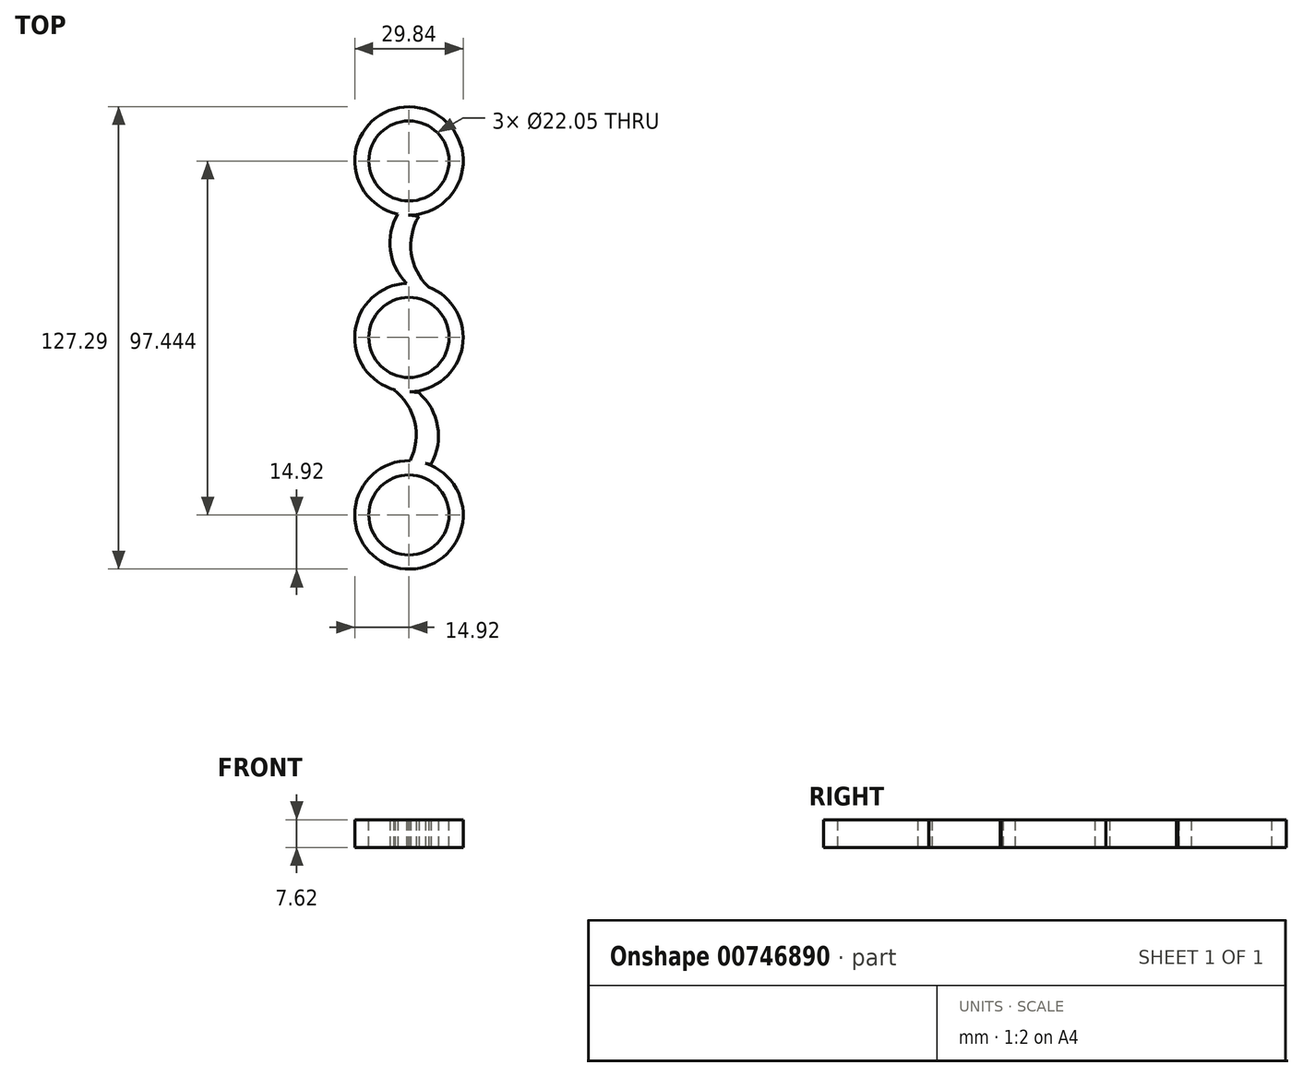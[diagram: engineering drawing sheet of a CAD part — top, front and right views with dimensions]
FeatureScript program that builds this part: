
annotation { "Feature Type Name" : "Feature", "Feature Type Description" : "" }
export const myFeature = defineFeature(function(context is Context, id is Id, definition is map)
    precondition{}
    {
        {
            var Q0;
            Q0=qCreatedBy(makeId("Top.planeOp"),FACE);
            var sketch = newSketch(context, id + "F0", { "sketchPlane" : qUnion([Q0])});
            skCircle(sketch, "E0", {"center": v(0, 0) * mm, "radius": 14.92 * mm});
            skSolve(sketch);
        }
        {
            var Q0;
            Q0 = qSketchRegion(id + "F0", true);
            extrude(context, id + "F1", {"entities" : qUnion([Q0]), "depth" : 7.62 * mm, "offsetDistance" : 25.4 * mm});
        }
        {
            var Q0;
            Q0=makeQuery(id+"F1.opExtrude","CAP_FACE",FACE,{"disambiguationData":[OSD([sQuery(id+"F0.wireOp",EDGE,"E0")])],"isStart":false});
            var sketch = newSketch(context, id + "F2", { "sketchPlane" : qUnion([Q0])});
            skCircle(sketch, "E1", {"center": v(0, 0) * mm, "radius": 11.02 * mm});
            skSolve(sketch);
        }
        {
            var Q0;
            Q0 = qSketchRegion(id + "F2", true);
            extrude(context, id + "F3", {"entities" : qUnion([Q0]), "operationType" : NewBodyOperationType.REMOVE, "oppositeDirection" : true, "depth" : 25.4 * mm, "offsetDistance" : 25.4 * mm});
        }
        {
            var Q0;
            Q0=qCreatedBy(makeId("Top.planeOp"),FACE);
            var sketch = newSketch(context, id + "F4", { "sketchPlane" : qUnion([Q0])});
            skArc(sketch, "E2", {"start": v(-3.03, 34.03) * mm, "mid": v(-5.06, 23.76) * mm, "end": v(-0.21, 14.49) * mm});
            skArc(sketch, "E3", {"start": v(2.7, 33.32) * mm, "mid": v(0.67, 23.06) * mm, "end": v(5.52, 13.78) * mm});
            skLineSegment(sketch, "E4", {"start": v(-3.03, 34.03) * mm, "end": v(2.7, 33.32) * mm});
            skLineSegment(sketch, "E5", {"start": v(-0.21, 14.49) * mm, "end": v(5.52, 13.78) * mm});
            skArc(sketch, "E6", {"start": v(6.11, -34.83) * mm, "mid": v(7.9, -24.42) * mm, "end": v(2.7, -15.22) * mm});
            skArc(sketch, "E7", {"start": v(0.23, -34.11) * mm, "mid": v(1.6, -23.44) * mm, "end": v(-4.2, -14.37) * mm});
            skLineSegment(sketch, "E8", {"start": v(6.11, -34.83) * mm, "end": v(0.23, -34.11) * mm});
            skLineSegment(sketch, "E9", {"start": v(2.7, -15.22) * mm, "end": v(-4.2, -14.37) * mm});
            skSolve(sketch);
        }
        {
            var Q0;
            Q0 = qSketchRegion(id + "F4", true);
            extrude(context, id + "F5", {"entities" : qUnion([Q0]), "operationType" : NewBodyOperationType.ADD, "depth" : 7.62 * mm, "offsetDistance" : 25.4 * mm});
        }
        {
            var Q0;
            Q0 = qSketchRegion(id + "F4", true);
            extrude(context, id + "F6", {"entities" : qUnion([Q0]), "operationType" : NewBodyOperationType.ADD, "depth" : 7.62 * mm, "offsetDistance" : 25.4 * mm});
        }
        {
            var Q0;
            Q0=qCreatedBy(makeId("Top.planeOp"),FACE);
            var sketch = newSketch(context, id + "F7", { "sketchPlane" : qUnion([Q0])});
            skCircle(sketch, "E10", {"center": v(0, 48.6) * mm, "radius": 14.92 * mm});
            skCircle(sketch, "E11", {"center": v(0, -48.85) * mm, "radius": 14.92 * mm});
            skSolve(sketch);
        }
        {
            var Q0;
            Q0 = qSketchRegion(id + "F7", true);
            extrude(context, id + "F8", {"entities" : qUnion([Q0]), "operationType" : NewBodyOperationType.ADD, "depth" : 7.62 * mm, "offsetDistance" : 25.4 * mm});
        }
        {
            var Q0;
            Q0=makeQuery(id+"F8.boolean.opBoolean","MERGE",FACE,{"derivedFrom":[makeQuery(id+"F5.boolean.opBoolean","MERGE",FACE,{"derivedFrom":[makeQuery(id+"F1.opExtrude","CAP_FACE",FACE,{"disambiguationData":[OSD([sQuery(id+"F0.wireOp",EDGE,"E0")])],"isStart":false}),makeQuery(id+"F5.opExtrude","CAP_FACE",FACE,{"disambiguationData":[OSD([sQuery(id+"F4.wireOp",EDGE,"E2"),sQuery(id+"F4.wireOp",EDGE,"E3"),sQuery(id+"F4.wireOp",EDGE,"E4"),sQuery(id+"F4.wireOp",EDGE,"E5")])],"isStart":false}),makeQuery(id+"F5.opExtrude","CAP_FACE",FACE,{"disambiguationData":[OSD([sQuery(id+"F4.wireOp",EDGE,"E6"),sQuery(id+"F4.wireOp",EDGE,"E7"),sQuery(id+"F4.wireOp",EDGE,"E8"),sQuery(id+"F4.wireOp",EDGE,"E9")])],"isStart":false})]}),makeQuery(id+"F8.opExtrude","CAP_FACE",FACE,{"disambiguationData":[OSD([sQuery(id+"F7.wireOp",EDGE,"E10")])],"isStart":false}),makeQuery(id+"F8.opExtrude","CAP_FACE",FACE,{"disambiguationData":[OSD([sQuery(id+"F7.wireOp",EDGE,"E11")])],"isStart":false})]});
            var sketch = newSketch(context, id + "F9", { "sketchPlane" : qUnion([Q0])});
            skCircle(sketch, "E12", {"center": v(0, 48.6) * mm, "radius": 11.02 * mm});
            skCircle(sketch, "E13", {"center": v(0, -48.85) * mm, "radius": 11.02 * mm});
            skSolve(sketch);
        }
        {
            var Q0;
            Q0 = qSketchRegion(id + "F9", true);
            extrude(context, id + "F10", {"entities" : qUnion([Q0]), "operationType" : NewBodyOperationType.REMOVE, "oppositeDirection" : true, "depth" : 25.4 * mm, "offsetDistance" : 25.4 * mm});
        }
    });
